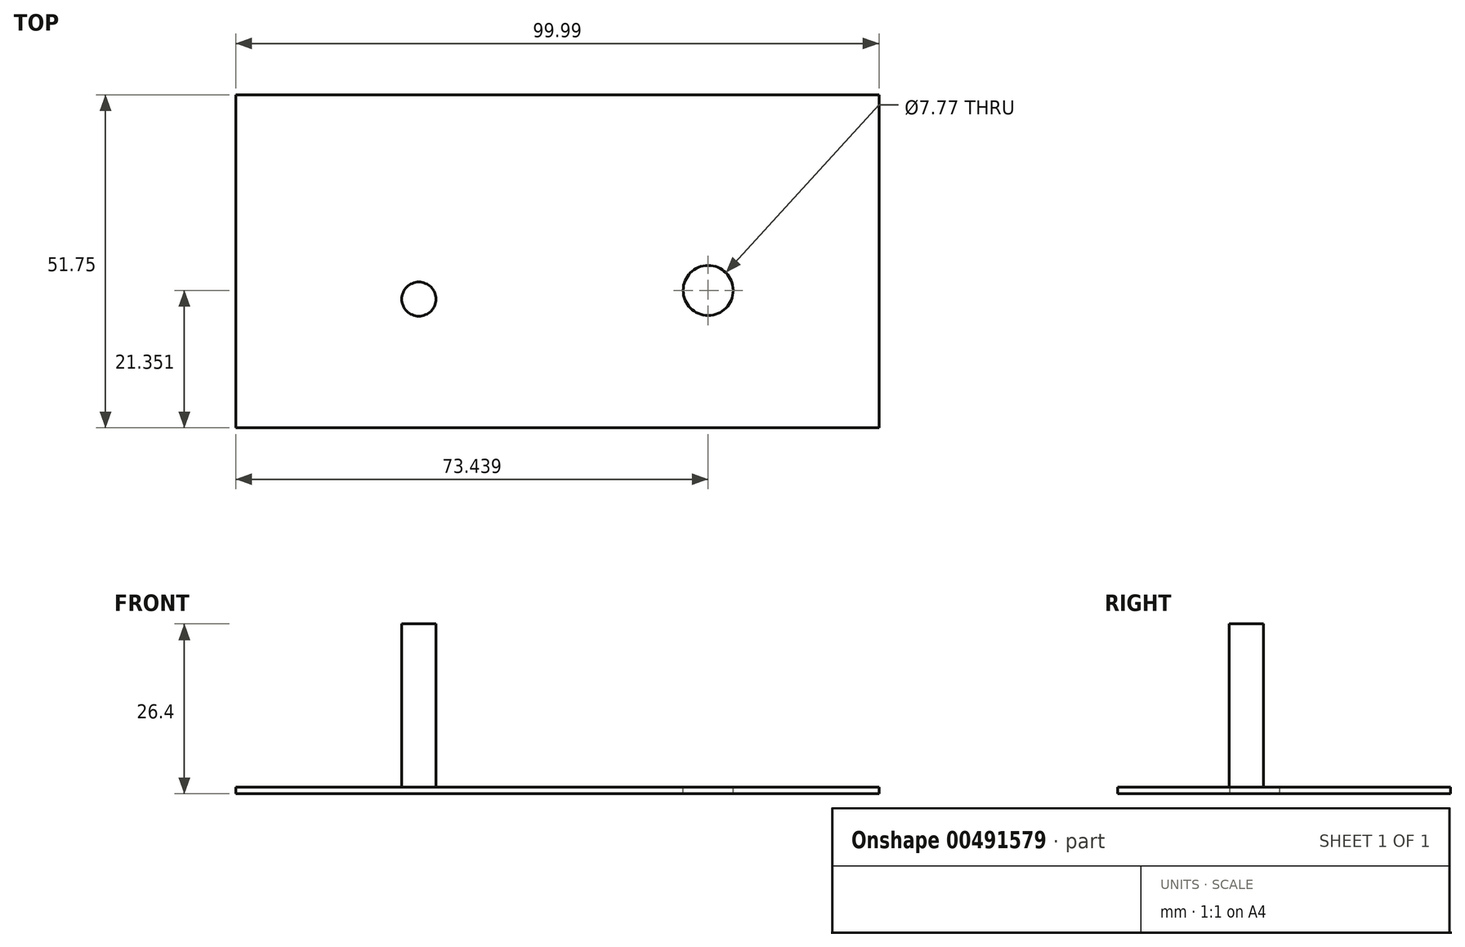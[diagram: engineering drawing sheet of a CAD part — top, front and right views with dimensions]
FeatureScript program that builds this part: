
annotation { "Feature Type Name" : "Feature", "Feature Type Description" : "" }
export const myFeature = defineFeature(function(context is Context, id is Id, definition is map)
    precondition{}
    {
        {
            var Q0;
            Q0=qCreatedBy(makeId("Top.planeOp"),FACE);
            var sketch = newSketch(context, id + "F0", { "sketchPlane" : qUnion([Q0])});
            skLineSegment(sketch, "E0.bottom", {"start": v(0, 0) * mm, "end": v(100, 0) * mm});
            skLineSegment(sketch, "E0.top", {"start": v(0, 51.75) * mm, "end": v(100, 51.75) * mm});
            skLineSegment(sketch, "E0.left", {"start": v(0, 0) * mm, "end": v(0, 51.75) * mm});
            skLineSegment(sketch, "E0.right", {"start": v(100, 0) * mm, "end": v(100, 51.75) * mm});
            skSolve(sketch);
        }
        {
            var Q0;
            Q0 = qSketchRegion(id + "F0", true);
            extrude(context, id + "F1", {"entities" : qUnion([Q0]), "depth" : 1 * mm});
        }
        {
            var Q0;
            Q0=makeQuery(id+"F1.opExtrude","CAP_FACE",FACE,{"disambiguationData":[OSD([sQuery(id+"F0.wireOp",EDGE,"E0.bottom"),sQuery(id+"F0.wireOp",EDGE,"E0.top"),sQuery(id+"F0.wireOp",EDGE,"E0.left"),sQuery(id+"F0.wireOp",EDGE,"E0.right")])],"isStart":false});
            var sketch = newSketch(context, id + "F2", { "sketchPlane" : qUnion([Q0])});
            skCircle(sketch, "E1", {"center": v(73.44, 21.35) * mm, "radius": 3.88 * mm});
            skSolve(sketch);
        }
        {
            var Q0;
            Q0 = qSketchRegion(id + "F2", true);
            extrude(context, id + "F3", {"entities" : qUnion([Q0]), "operationType" : NewBodyOperationType.REMOVE, "endBound" : BoundingType.THROUGH_ALL, "oppositeDirection" : true, "depth" : 25.4 * mm});
        }
        {
            var Q0;
            Q0=makeQuery(id+"F1.opExtrude","CAP_FACE",FACE,{"disambiguationData":[OSD([sQuery(id+"F0.wireOp",EDGE,"E0.bottom"),sQuery(id+"F0.wireOp",EDGE,"E0.top"),sQuery(id+"F0.wireOp",EDGE,"E0.left"),sQuery(id+"F0.wireOp",EDGE,"E0.right")])],"isStart":false});
            var sketch = newSketch(context, id + "F4", { "sketchPlane" : qUnion([Q0])});
            skCircle(sketch, "E2", {"center": v(28.46, 20) * mm, "radius": 2.65 * mm});
            skSolve(sketch);
        }
        {
            var Q0;
            Q0 = qSketchRegion(id + "F4", true);
            extrude(context, id + "F5", {"entities" : qUnion([Q0]), "operationType" : NewBodyOperationType.ADD, "depth" : 25.4 * mm});
        }
    });
